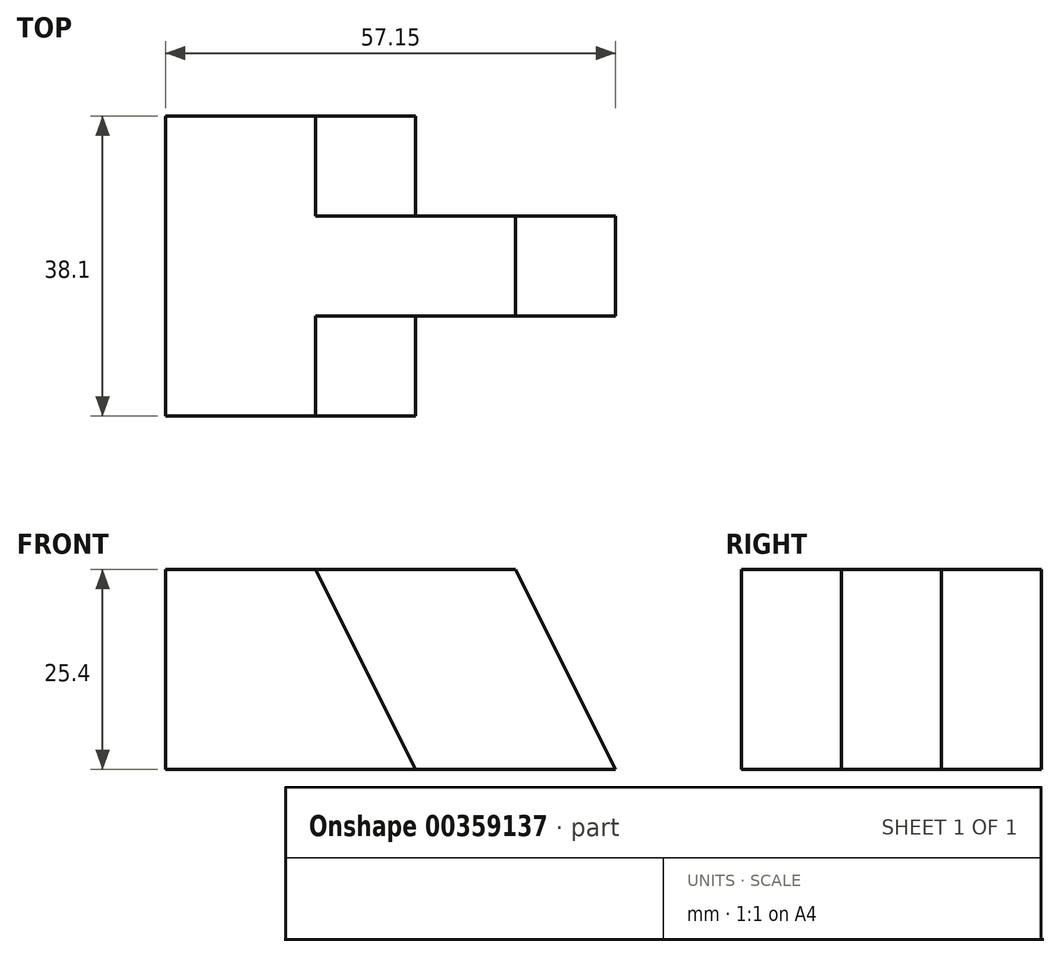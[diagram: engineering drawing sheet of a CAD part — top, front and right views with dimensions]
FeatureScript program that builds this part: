
annotation { "Feature Type Name" : "Feature", "Feature Type Description" : "" }
export const myFeature = defineFeature(function(context is Context, id is Id, definition is map)
    precondition{}
    {
        {
            var Q0;
            Q0=qCreatedBy(makeId("Front.planeOp"),FACE);
            var sketch = newSketch(context, id + "F0", { "sketchPlane" : qUnion([Q0])});
            skLineSegment(sketch, "E0", {"start": v(-32.43, 24.6) * mm, "end": v(-32.43, -0.8) * mm});
            skLineSegment(sketch, "E1", {"start": v(-32.43, -0.8) * mm, "end": v(12.02, -0.8) * mm});
            skLineSegment(sketch, "E2", {"start": v(12.02, -0.8) * mm, "end": v(12.02, 24.6) * mm});
            skLineSegment(sketch, "E3", {"start": v(12.02, 24.6) * mm, "end": v(-32.43, 24.6) * mm});
            skSolve(sketch);
        }
        {
            var Q0;
            Q0 = qSketchRegion(id + "F0", true);
            extrude(context, id + "F1", {"entities" : qUnion([Q0]), "depth" : 12.7 * mm});
        }
        {
            var Q0;
            Q0=makeQuery(id+"F1.opExtrude","CAP_FACE",FACE,{"disambiguationData":[OSD([sQuery(id+"F0.wireOp",EDGE,"E0"),sQuery(id+"F0.wireOp",EDGE,"E1"),sQuery(id+"F0.wireOp",EDGE,"E2"),sQuery(id+"F0.wireOp",EDGE,"E3")])],"isStart":false});
            var sketch = newSketch(context, id + "F2", { "sketchPlane" : qUnion([Q0])});
            skLineSegment(sketch, "E4", {"start": v(-32.43, 24.6) * mm, "end": v(-32.43, -0.8) * mm});
            skLineSegment(sketch, "E5", {"start": v(-32.43, -0.8) * mm, "end": v(-0.68, -0.8) * mm});
            skLineSegment(sketch, "E6", {"start": v(-0.68, -0.8) * mm, "end": v(-13.38, 24.6) * mm});
            skLineSegment(sketch, "E7", {"start": v(-13.38, 24.6) * mm, "end": v(-32.43, 24.6) * mm});
            skSolve(sketch);
        }
        {
            var Q0;
            Q0=makeQuery(id+"F1.opExtrude","CAP_FACE",FACE,{"disambiguationData":[OSD([sQuery(id+"F0.wireOp",EDGE,"E0"),sQuery(id+"F0.wireOp",EDGE,"E1"),sQuery(id+"F0.wireOp",EDGE,"E2"),sQuery(id+"F0.wireOp",EDGE,"E3")])],"isStart":true});
            var sketch = newSketch(context, id + "F3", { "sketchPlane" : qUnion([Q0])});
            skLineSegment(sketch, "E8", {"start": v(32.43, 24.6) * mm, "end": v(13.38, 24.6) * mm});
            skLineSegment(sketch, "E9", {"start": v(13.38, 24.6) * mm, "end": v(0.68, -0.8) * mm});
            skLineSegment(sketch, "E10", {"start": v(0.68, -0.8) * mm, "end": v(32.43, -0.8) * mm});
            skLineSegment(sketch, "E11", {"start": v(32.43, -0.8) * mm, "end": v(32.43, 24.6) * mm});
            skSolve(sketch);
        }
        {
            var Q0;
            Q0 = qSketchRegion(id + "F3", true);
            extrude(context, id + "F4", {"entities" : qUnion([Q0]), "operationType" : NewBodyOperationType.ADD, "depth" : 12.7 * mm});
        }
        {
            var Q0;
            Q0=makeQuery(id+"F2.imprint","IMPRINT",FACE,{"disambiguationData":[TD([[makeQuery(id+"F2.imprint","IMPRINT",EDGE,{"derivedFrom":sQuery(id+"F2.wireOp",EDGE,"E4")}),1.0]])]});
            extrude(context, id + "F5", {"entities" : qUnion([Q0]), "operationType" : NewBodyOperationType.ADD, "depth" : 12.7 * mm});
        }
        {
            var Q0;
            Q0=makeQuery(id+"F1.opExtrude","CAP_FACE",FACE,{"disambiguationData":[OSD([sQuery(id+"F0.wireOp",EDGE,"E0"),sQuery(id+"F0.wireOp",EDGE,"E1"),sQuery(id+"F0.wireOp",EDGE,"E2"),sQuery(id+"F0.wireOp",EDGE,"E3")])],"isStart":false});
            var sketch = newSketch(context, id + "F6", { "sketchPlane" : qUnion([Q0])});
            skLineSegment(sketch, "E12", {"start": v(12.02, 24.6) * mm, "end": v(12.02, -0.8) * mm});
            skLineSegment(sketch, "E13", {"start": v(12.02, -0.8) * mm, "end": v(24.72, -0.8) * mm});
            skLineSegment(sketch, "E14", {"start": v(24.72, -0.8) * mm, "end": v(12.02, 24.6) * mm});
            skSolve(sketch);
        }
        {
            var Q0;
            Q0=makeQuery(id+"F6.imprint","IMPRINT",FACE,{"disambiguationData":[TD([[makeQuery(id+"F6.imprint","IMPRINT",EDGE,{"derivedFrom":sQuery(id+"F6.wireOp",EDGE,"E12")}),-1.0]])]});
            extrude(context, id + "F7", {"entities" : qUnion([Q0]), "operationType" : NewBodyOperationType.ADD, "oppositeDirection" : true, "depth" : 12.7 * mm});
        }
    });
